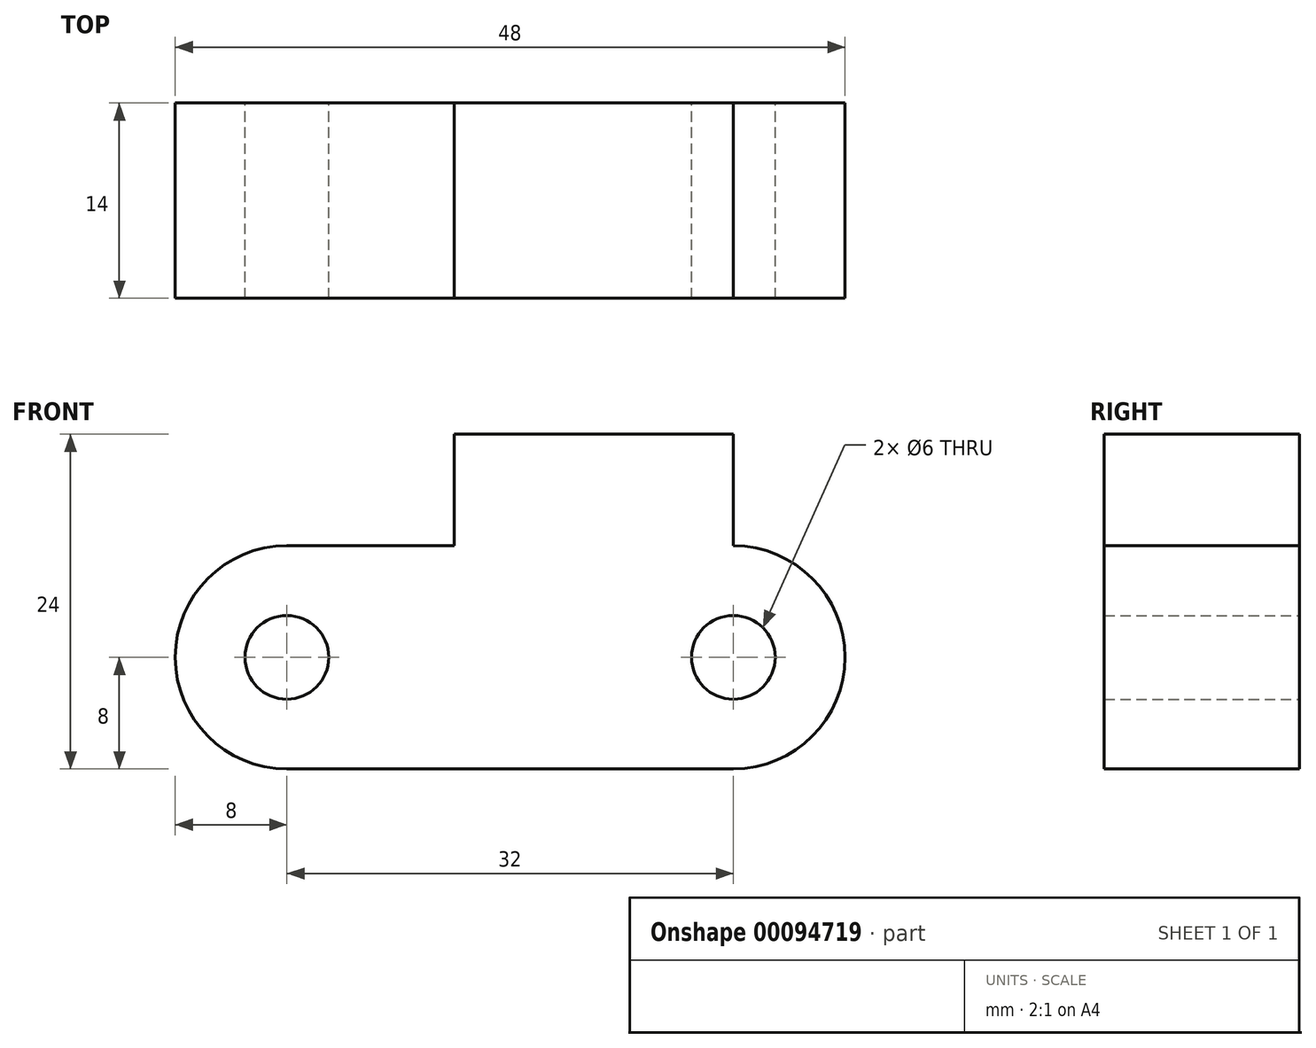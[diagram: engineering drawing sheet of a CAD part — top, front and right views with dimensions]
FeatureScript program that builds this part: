
annotation { "Feature Type Name" : "Feature", "Feature Type Description" : "" }
export const myFeature = defineFeature(function(context is Context, id is Id, definition is map)
    precondition{}
    {
        {
            var Q0;
            Q0=qCreatedBy(makeId("Front.planeOp"),FACE);
            var sketch = newSketch(context, id + "F0", { "sketchPlane" : qUnion([Q0])});
            skCircle(sketch, "E0", {"center": v(0, 0) * mm, "radius": 3 * mm});
            skCircle(sketch, "E1.1.0.0", {"center": v(-32, 0) * mm, "radius": 3 * mm});
            skLineSegment(sketch, "E1.direction1", {"start": v(0, 0) * mm, "end": v(-32, 0) * mm, "construction": true});
            skArc(sketch, "E2", {"start": v(-32, 8) * mm, "mid": v(-40, 0) * mm, "end": v(-32, -8) * mm});
            skArc(sketch, "E3", {"start": v(0, -8) * mm, "mid": v(8, 0) * mm, "end": v(0, 8) * mm});
            skLineSegment(sketch, "E4", {"start": v(0, -8) * mm, "end": v(-32, -8) * mm});
            skLineSegment(sketch, "E5", {"start": v(0, 8) * mm, "end": v(0, 16) * mm});
            skLineSegment(sketch, "E6", {"start": v(0, 16) * mm, "end": v(-20, 16) * mm});
            skLineSegment(sketch, "E7", {"start": v(-20, 16) * mm, "end": v(-20, 8) * mm});
            skLineSegment(sketch, "E8", {"start": v(-20, 8) * mm, "end": v(-32, 8) * mm});
            skSolve(sketch);
        }
        {
            var Q0;
            Q0 = qSketchRegion(id + "F0", true);
            extrude(context, id + "F1", {"entities" : qUnion([Q0]), "depth" : 14 * mm});
        }
    });
